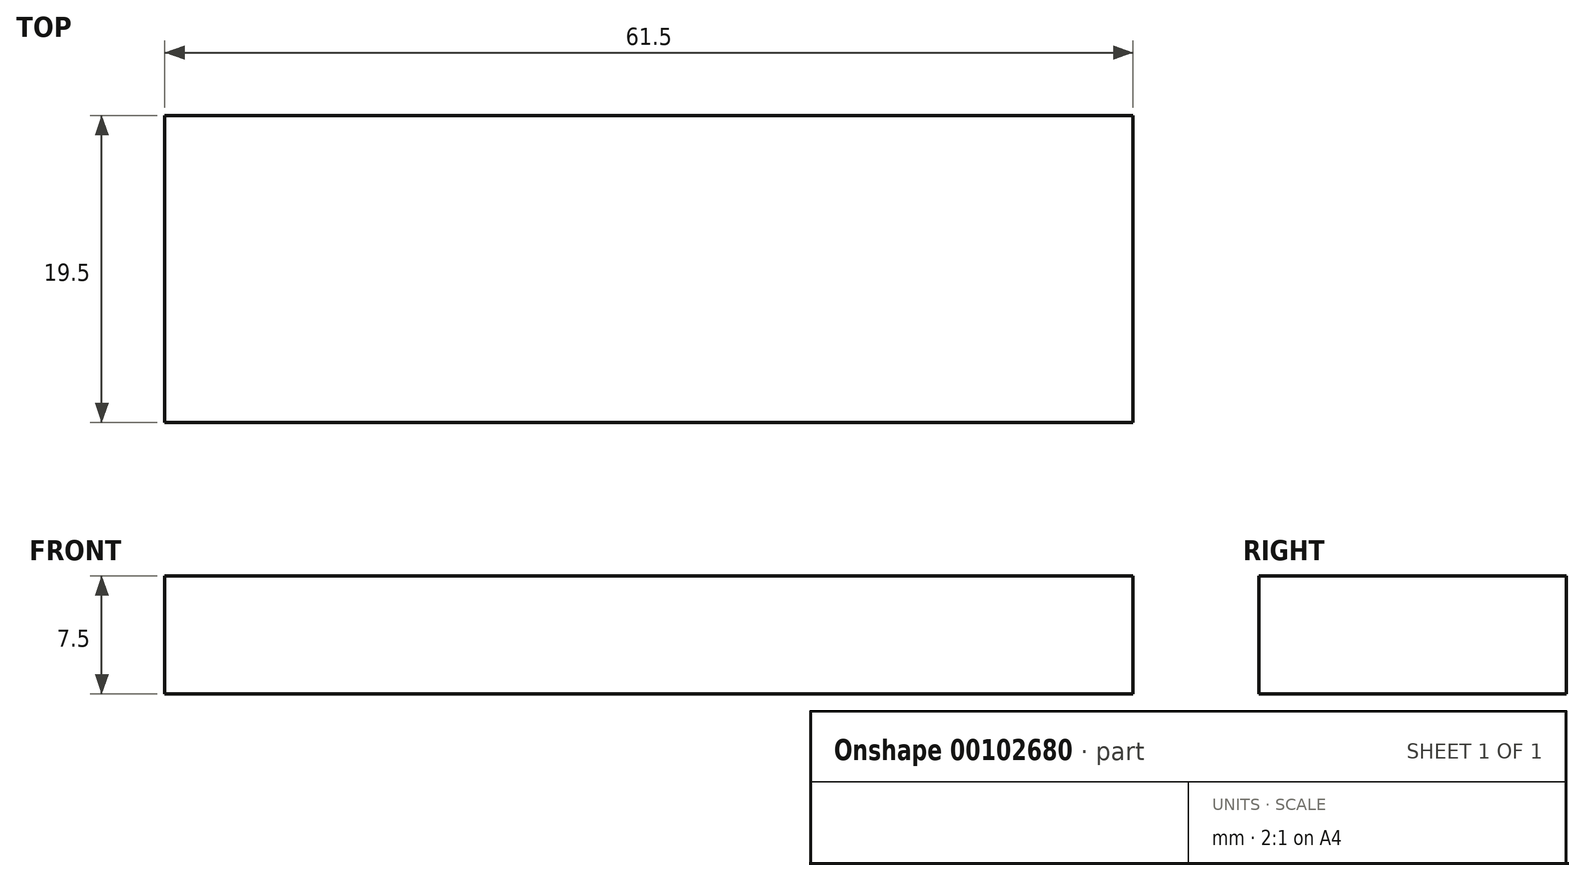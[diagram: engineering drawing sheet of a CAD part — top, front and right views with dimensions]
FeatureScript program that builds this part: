
annotation { "Feature Type Name" : "Feature", "Feature Type Description" : "" }
export const myFeature = defineFeature(function(context is Context, id is Id, definition is map)
    precondition{}
    {
        {
            var Q0;
            Q0=qCreatedBy(makeId("Top.planeOp"),FACE);
            var sketch = newSketch(context, id + "F0", { "sketchPlane" : qUnion([Q0])});
            skLineSegment(sketch, "E0.bottom", {"start": v(30.75, 9.75) * mm, "end": v(-30.75, 9.75) * mm});
            skLineSegment(sketch, "E0.top", {"start": v(30.75, -9.75) * mm, "end": v(-30.75, -9.75) * mm});
            skLineSegment(sketch, "E0.left", {"start": v(30.75, 9.75) * mm, "end": v(30.75, -9.75) * mm});
            skLineSegment(sketch, "E0.right", {"start": v(-30.75, 9.75) * mm, "end": v(-30.75, -9.75) * mm});
            skPoint(sketch, "E0.middle", {"position": v(0, 0) * mm});
            skSolve(sketch);
        }
        {
            var Q0;
            Q0=makeQuery(id+"F0.imprint","IMPRINT",FACE,{"disambiguationData":[TD([[makeQuery(id+"F0.imprint","IMPRINT",EDGE,{"derivedFrom":sQuery(id+"F0.wireOp",EDGE,"E0.bottom")}),1.0]])]});
            extrude(context, id + "F1", {"entities" : qUnion([Q0]), "depth" : 7.5 * mm});
        }
    });
